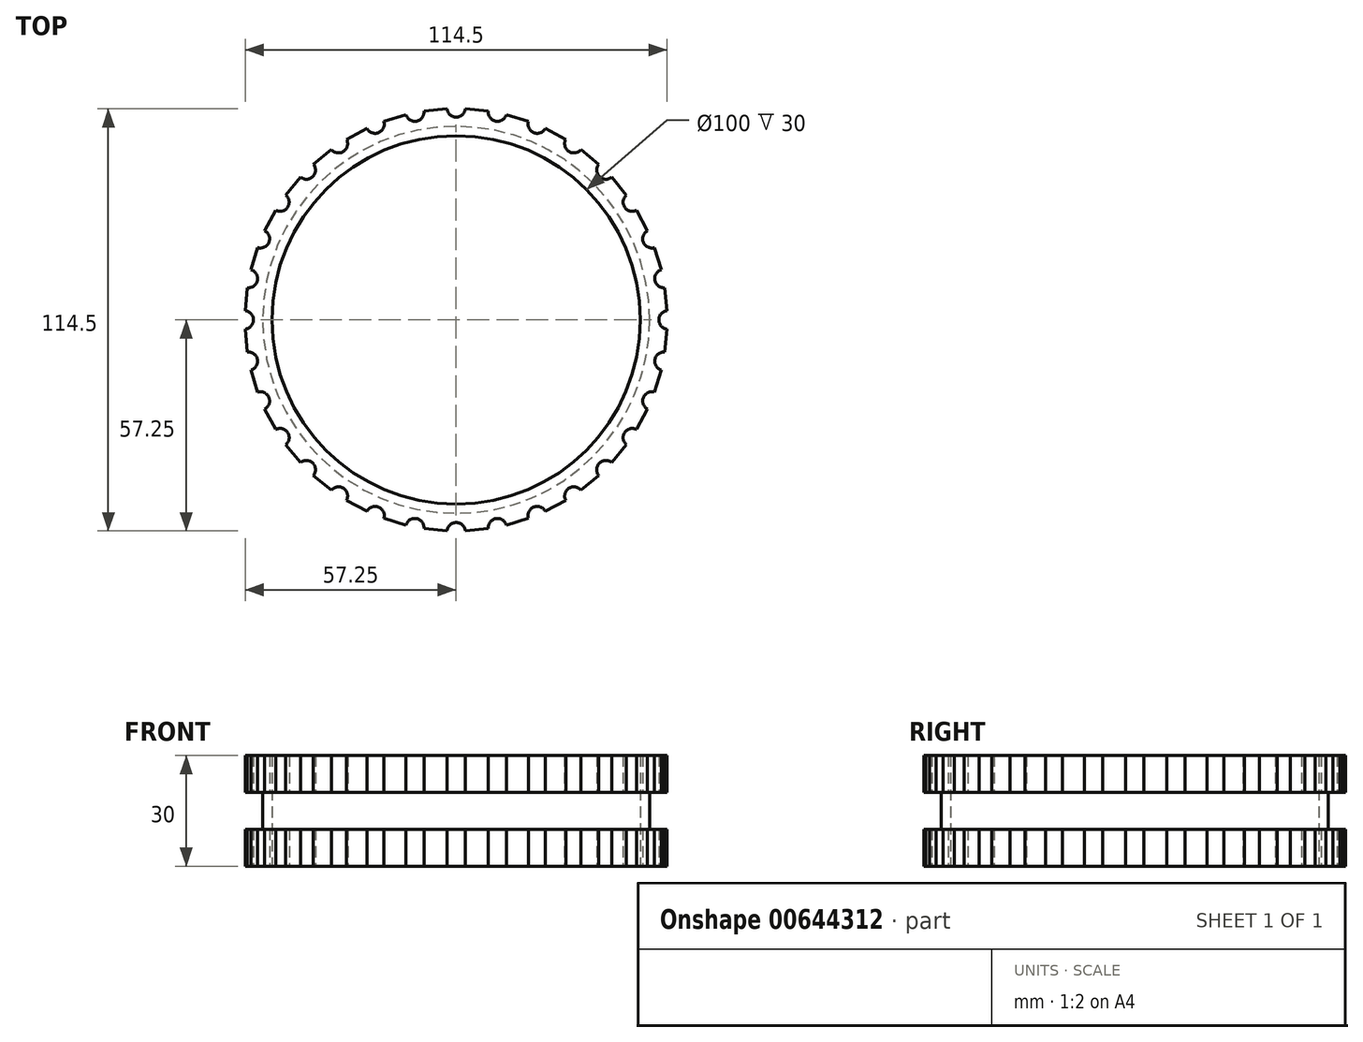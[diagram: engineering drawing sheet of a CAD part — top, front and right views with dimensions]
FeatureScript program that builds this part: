
annotation { "Feature Type Name" : "Feature", "Feature Type Description" : "" }
export const myFeature = defineFeature(function(context is Context, id is Id, definition is map)
    precondition{}
    {
        {
            var Q0;
            Q0=qCreatedBy(makeId("Top.planeOp"),FACE);
            var sketch = newSketch(context, id + "F0", { "sketchPlane" : qUnion([Q0])});
            skCircle(sketch, "E0", {"center": v(0, 0) * mm, "radius": 50 * mm});
            skCircle(sketch, "E1", {"center": v(0, 0) * mm, "radius": 52.5 * mm});
            skCircle(sketch, "E2", {"center": v(0, 0) * mm, "radius": 55 * mm});
            skCircle(sketch, "E3", {"center": v(0, 0) * mm, "radius": 60 * mm});
            skCircle(sketch, "E4", {"center": v(0, 0) * mm, "radius": 57.5 * mm});
            skCircle(sketch, "E5", {"center": v(-57.5, 0) * mm, "radius": 2.5 * mm});
            skCircle(sketch, "E6", {"center": v(0, 57.5) * mm, "radius": 2.5 * mm});
            skCircle(sketch, "E7", {"center": v(57.5, 0) * mm, "radius": 2.5 * mm});
            skCircle(sketch, "E8", {"center": v(0, -57.5) * mm, "radius": 2.5 * mm});
            skCircle(sketch, "E9.cCircle", {"center": v(0, 0) * mm, "radius": 57.5 * mm, "construction": true});
            skLineSegment(sketch, "E9.0", {"start": v(0, -57.5) * mm, "end": v(-11.22, -56.4) * mm});
            skLineSegment(sketch, "E9.1", {"start": v(-11.22, -56.4) * mm, "end": v(-22, -53.12) * mm});
            skLineSegment(sketch, "E9.2", {"start": v(-22, -53.12) * mm, "end": v(-31.95, -47.8) * mm});
            skLineSegment(sketch, "E9.3", {"start": v(-31.95, -47.8) * mm, "end": v(-40.66, -40.66) * mm});
            skLineSegment(sketch, "E9.4", {"start": v(-40.66, -40.66) * mm, "end": v(-47.8, -31.95) * mm});
            skLineSegment(sketch, "E9.5", {"start": v(-47.8, -31.95) * mm, "end": v(-53.12, -22) * mm});
            skLineSegment(sketch, "E9.6", {"start": v(-53.12, -22) * mm, "end": v(-56.4, -11.22) * mm});
            skLineSegment(sketch, "E9.7", {"start": v(-56.4, -11.22) * mm, "end": v(-57.5, 0) * mm});
            skLineSegment(sketch, "E9.8", {"start": v(-57.5, 0) * mm, "end": v(-56.4, 11.22) * mm});
            skLineSegment(sketch, "E9.9", {"start": v(-56.4, 11.22) * mm, "end": v(-53.12, 22) * mm});
            skLineSegment(sketch, "E9.10", {"start": v(-53.12, 22) * mm, "end": v(-47.8, 31.95) * mm});
            skLineSegment(sketch, "E9.11", {"start": v(-47.8, 31.95) * mm, "end": v(-40.66, 40.66) * mm});
            skLineSegment(sketch, "E9.12", {"start": v(-40.66, 40.66) * mm, "end": v(-31.95, 47.8) * mm});
            skLineSegment(sketch, "E9.13", {"start": v(-31.95, 47.8) * mm, "end": v(-22, 53.12) * mm});
            skLineSegment(sketch, "E9.14", {"start": v(-22, 53.12) * mm, "end": v(-11.22, 56.4) * mm});
            skLineSegment(sketch, "E9.15", {"start": v(-11.22, 56.4) * mm, "end": v(0, 57.5) * mm});
            skLineSegment(sketch, "E9.16", {"start": v(0, 57.5) * mm, "end": v(11.22, 56.4) * mm});
            skLineSegment(sketch, "E9.17", {"start": v(11.22, 56.4) * mm, "end": v(22, 53.12) * mm});
            skLineSegment(sketch, "E9.18", {"start": v(22, 53.12) * mm, "end": v(31.95, 47.8) * mm});
            skLineSegment(sketch, "E9.19", {"start": v(31.95, 47.8) * mm, "end": v(40.66, 40.66) * mm});
            skLineSegment(sketch, "E9.20", {"start": v(40.66, 40.66) * mm, "end": v(47.8, 31.95) * mm});
            skLineSegment(sketch, "E9.21", {"start": v(47.8, 31.95) * mm, "end": v(53.12, 22) * mm});
            skLineSegment(sketch, "E9.22", {"start": v(53.12, 22) * mm, "end": v(56.4, 11.22) * mm});
            skLineSegment(sketch, "E9.23", {"start": v(56.4, 11.22) * mm, "end": v(57.5, 0) * mm});
            skLineSegment(sketch, "E9.24", {"start": v(57.5, 0) * mm, "end": v(56.4, -11.22) * mm});
            skLineSegment(sketch, "E9.25", {"start": v(56.4, -11.22) * mm, "end": v(53.12, -22) * mm});
            skLineSegment(sketch, "E9.26", {"start": v(53.12, -22) * mm, "end": v(47.8, -31.95) * mm});
            skLineSegment(sketch, "E9.27", {"start": v(47.8, -31.95) * mm, "end": v(40.66, -40.66) * mm});
            skLineSegment(sketch, "E9.28", {"start": v(40.66, -40.66) * mm, "end": v(31.95, -47.8) * mm});
            skLineSegment(sketch, "E9.29", {"start": v(31.95, -47.8) * mm, "end": v(22, -53.12) * mm});
            skLineSegment(sketch, "E9.30", {"start": v(22, -53.12) * mm, "end": v(11.22, -56.4) * mm});
            skLineSegment(sketch, "E9.31", {"start": v(11.22, -56.4) * mm, "end": v(0, -57.5) * mm});
            skCircle(sketch, "E10", {"center": v(-11.22, -56.4) * mm, "radius": 2.5 * mm});
            skCircle(sketch, "E11", {"center": v(-22, -53.12) * mm, "radius": 2.5 * mm});
            skCircle(sketch, "E12", {"center": v(-31.95, -47.8) * mm, "radius": 2.5 * mm});
            skCircle(sketch, "E13", {"center": v(-40.66, -40.66) * mm, "radius": 2.5 * mm});
            skCircle(sketch, "E14", {"center": v(-47.8, -31.95) * mm, "radius": 2.5 * mm});
            skCircle(sketch, "E15", {"center": v(-53.12, -22) * mm, "radius": 2.5 * mm});
            skCircle(sketch, "E16", {"center": v(-56.4, -11.22) * mm, "radius": 2.5 * mm});
            skCircle(sketch, "E17", {"center": v(-56.4, 11.22) * mm, "radius": 2.5 * mm});
            skCircle(sketch, "E18", {"center": v(-53.12, 22) * mm, "radius": 2.5 * mm});
            skCircle(sketch, "E19", {"center": v(-47.8, 31.95) * mm, "radius": 2.5 * mm});
            skCircle(sketch, "E20", {"center": v(-40.66, 40.66) * mm, "radius": 2.5 * mm});
            skCircle(sketch, "E21", {"center": v(-31.95, 47.8) * mm, "radius": 2.5 * mm});
            skCircle(sketch, "E22", {"center": v(-22, 53.12) * mm, "radius": 2.5 * mm});
            skCircle(sketch, "E23", {"center": v(-11.22, 56.4) * mm, "radius": 2.5 * mm});
            skCircle(sketch, "E24.MirrorC", {"center": v(11.22, -56.4) * mm, "radius": 2.5 * mm});
            skCircle(sketch, "E25.MirrorC", {"center": v(22, -53.12) * mm, "radius": 2.5 * mm});
            skCircle(sketch, "E26.MirrorC", {"center": v(31.95, -47.8) * mm, "radius": 2.5 * mm});
            skCircle(sketch, "E27.MirrorC", {"center": v(40.66, -40.66) * mm, "radius": 2.5 * mm});
            skCircle(sketch, "E28.MirrorC", {"center": v(53.12, -22) * mm, "radius": 2.5 * mm});
            skCircle(sketch, "E29.MirrorC", {"center": v(56.4, -11.22) * mm, "radius": 2.5 * mm});
            skCircle(sketch, "E30.MirrorC", {"center": v(56.4, 11.22) * mm, "radius": 2.5 * mm});
            skCircle(sketch, "E31.MirrorC", {"center": v(53.12, 22) * mm, "radius": 2.5 * mm});
            skCircle(sketch, "E32.MirrorC", {"center": v(47.8, 31.95) * mm, "radius": 2.5 * mm});
            skCircle(sketch, "E33.MirrorC", {"center": v(40.66, 40.66) * mm, "radius": 2.5 * mm});
            skCircle(sketch, "E34.MirrorC", {"center": v(31.95, 47.8) * mm, "radius": 2.5 * mm});
            skCircle(sketch, "E35.MirrorC", {"center": v(22, 53.12) * mm, "radius": 2.5 * mm});
            skCircle(sketch, "E36.MirrorC", {"center": v(11.22, 56.4) * mm, "radius": 2.5 * mm});
            skCircle(sketch, "E37.MirrorC", {"center": v(47.8, -31.95) * mm, "radius": 2.5 * mm});
            skSolve(sketch);
        }
        {
            var Q0;
            Q0=makeQuery(id+"F0.imprint","IMPRINT",FACE,{"disambiguationData":[TD([[makeQuery(id+"F0.imprint","IMPRINT",EDGE,{"derivedFrom":sQuery(id+"F0.wireOp",EDGE,"E1")}),-1.0]])]});
            var Q1;
            Q1=makeQuery(id+"F0.imprint","IMPRINT",FACE,{"disambiguationData":[TD([[makeQuery(id+"F0.imprint","IMPRINT",EDGE,{"derivedFrom":sQuery(id+"F0.wireOp",EDGE,"E2")}),-1.0]])]});
            extrude(context, id + "F1", {"entities" : qUnion([Q0, Q1]), "depth" : 10 * mm, "offsetDistance" : 25.4 * mm});
        }
        {
            var Q0;
            Q0=makeQuery(id+"F0.imprint","IMPRINT",FACE,{"disambiguationData":[TD([[makeQuery(id+"F0.imprint","IMPRINT",EDGE,{"derivedFrom":sQuery(id+"F0.wireOp",EDGE,"E0")}),-1.0]])]});
            extrude(context, id + "F2", {"entities" : qUnion([Q0]), "operationType" : NewBodyOperationType.ADD, "depth" : 30 * mm, "offsetDistance" : 25.4 * mm});
        }
        {
            var Q0;
            Q0=makeQuery(id+"F1.opExtrude","CAP_FACE",FACE,{"disambiguationData":[OSD([sQuery(id+"F0.wireOp",EDGE,"E1"),sQuery(id+"F0.wireOp",EDGE,"E3")])],"isStart":false});
            extrude(context, id + "F3", {"entities" : qUnion([Q0]), "operationType" : NewBodyOperationType.ADD, "depth" : 20 * mm, "offsetDistance" : 25.4 * mm, "hasSecondDirection" : true, "secondDirectionOppositeDirection" : false, "secondDirectionDepth" : 10 * mm});
        }
    });
